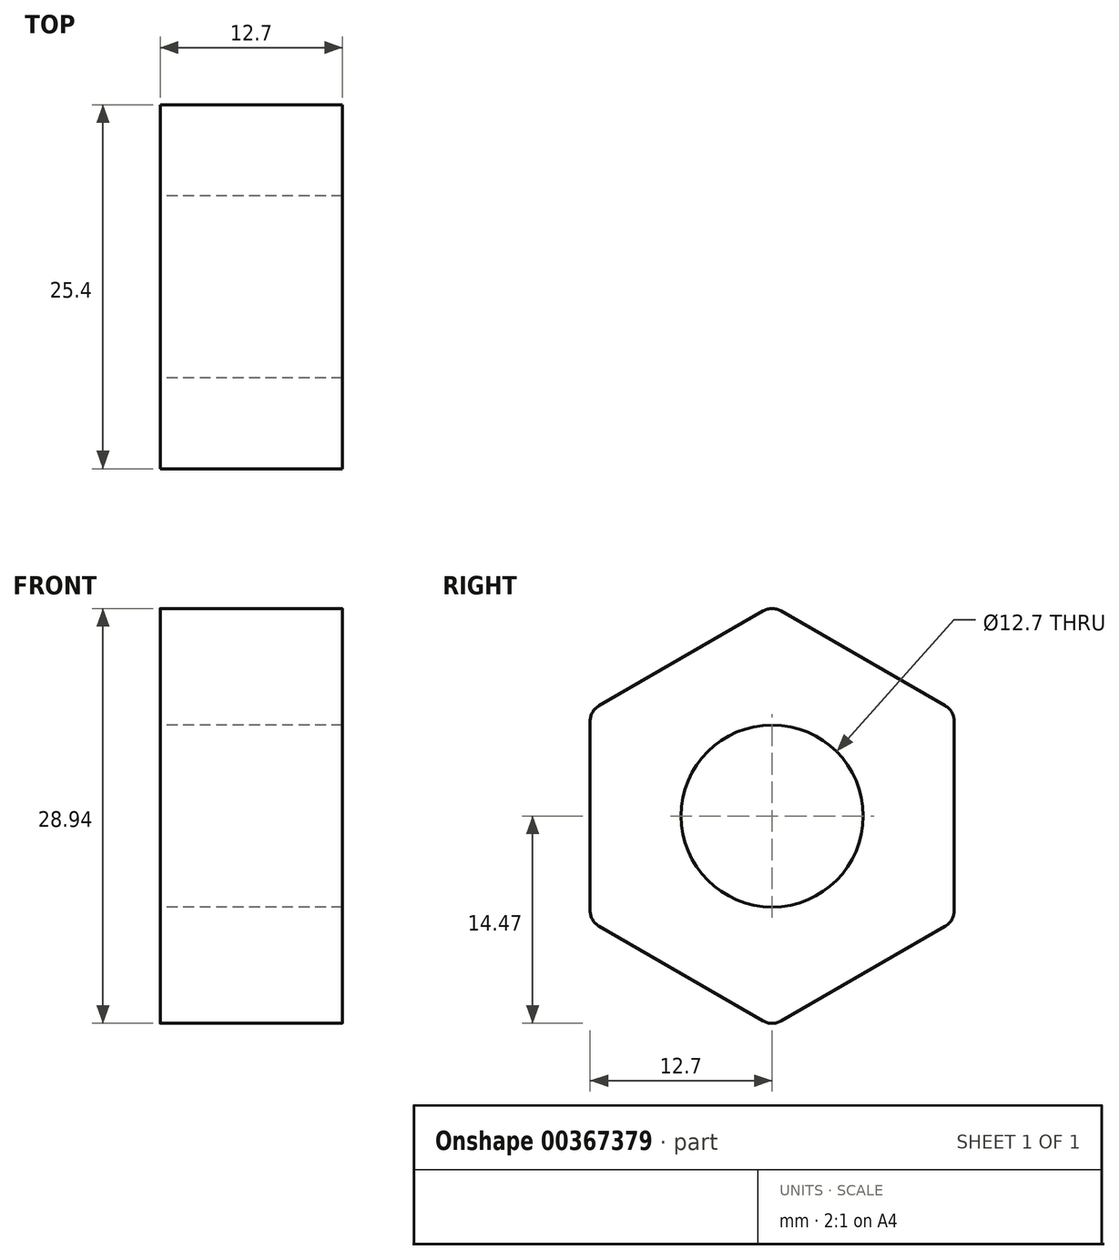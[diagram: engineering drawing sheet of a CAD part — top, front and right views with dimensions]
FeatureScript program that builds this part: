
annotation { "Feature Type Name" : "Feature", "Feature Type Description" : "" }
export const myFeature = defineFeature(function(context is Context, id is Id, definition is map)
    precondition{}
    {
        {
            var Q0;
            Q0=qCreatedBy(makeId("Right.planeOp"),FACE);
            var sketch = newSketch(context, id + "F0", { "sketchPlane" : qUnion([Q0])});
            skLineSegment(sketch, "E0", {"start": v(0, 14.66) * mm, "end": v(12.7, 7.33) * mm});
            skLineSegment(sketch, "E1", {"start": v(12.7, 7.33) * mm, "end": v(12.7, -7.33) * mm});
            skLineSegment(sketch, "E2", {"start": v(12.7, -7.33) * mm, "end": v(0, -14.66) * mm});
            skLineSegment(sketch, "E3", {"start": v(0, -14.66) * mm, "end": v(-12.7, -7.33) * mm});
            skLineSegment(sketch, "E4", {"start": v(-12.7, -7.33) * mm, "end": v(-12.7, 7.33) * mm});
            skLineSegment(sketch, "E5", {"start": v(-12.7, 7.33) * mm, "end": v(0, 14.66) * mm});
            skCircle(sketch, "E6", {"center": v(0, 0) * mm, "radius": 12.7 * mm, "construction": true});
            skCircle(sketch, "E7", {"center": v(0, 0) * mm, "radius": 6.35 * mm});
            skSolve(sketch);
        }
        {
            var Q0;
            Q0 = qSketchRegion(id + "F0", true);
            extrude(context, id + "F1", {"entities" : qUnion([Q0]), "depth" : 12.7 * mm});
        }
        {
            var Q0;
            Q0=makeQuery(id+"F1.opExtrude","SWEPT_EDGE",EDGE,{"disambiguationData":[OSD([sQuery(id+"F0.wireOp",EDGE,"E3"),sQuery(id+"F0.wireOp",EDGE,"E4")])]});
            var Q1;
            Q1=makeQuery(id+"F1.opExtrude","SWEPT_EDGE",EDGE,{"disambiguationData":[OSD([sQuery(id+"F0.wireOp",EDGE,"E4"),sQuery(id+"F0.wireOp",EDGE,"E5")])]});
            var Q2;
            Q2=makeQuery(id+"F1.opExtrude","SWEPT_EDGE",EDGE,{"disambiguationData":[OSD([sQuery(id+"F0.wireOp",EDGE,"E2"),sQuery(id+"F0.wireOp",EDGE,"E3")])]});
            var Q3;
            Q3=makeQuery(id+"F1.opExtrude","SWEPT_EDGE",EDGE,{"disambiguationData":[OSD([sQuery(id+"F0.wireOp",EDGE,"E1"),sQuery(id+"F0.wireOp",EDGE,"E2")])]});
            var Q4;
            Q4=makeQuery(id+"F1.opExtrude","SWEPT_EDGE",EDGE,{"disambiguationData":[OSD([sQuery(id+"F0.wireOp",EDGE,"E0"),sQuery(id+"F0.wireOp",EDGE,"E1")])]});
            var Q5;
            Q5=makeQuery(id+"F1.opExtrude","SWEPT_EDGE",EDGE,{"disambiguationData":[OSD([sQuery(id+"F0.wireOp",EDGE,"E0"),sQuery(id+"F0.wireOp",EDGE,"E5")])]});
            fillet(context, id + "F2", {"entities" : qUnion([Q0, Q1, Q2, Q3, Q4, Q5]), "radius" : 1.27 * mm, "tangentPropagation" : true, "allowEdgeOverflow" : false});
        }
    });
